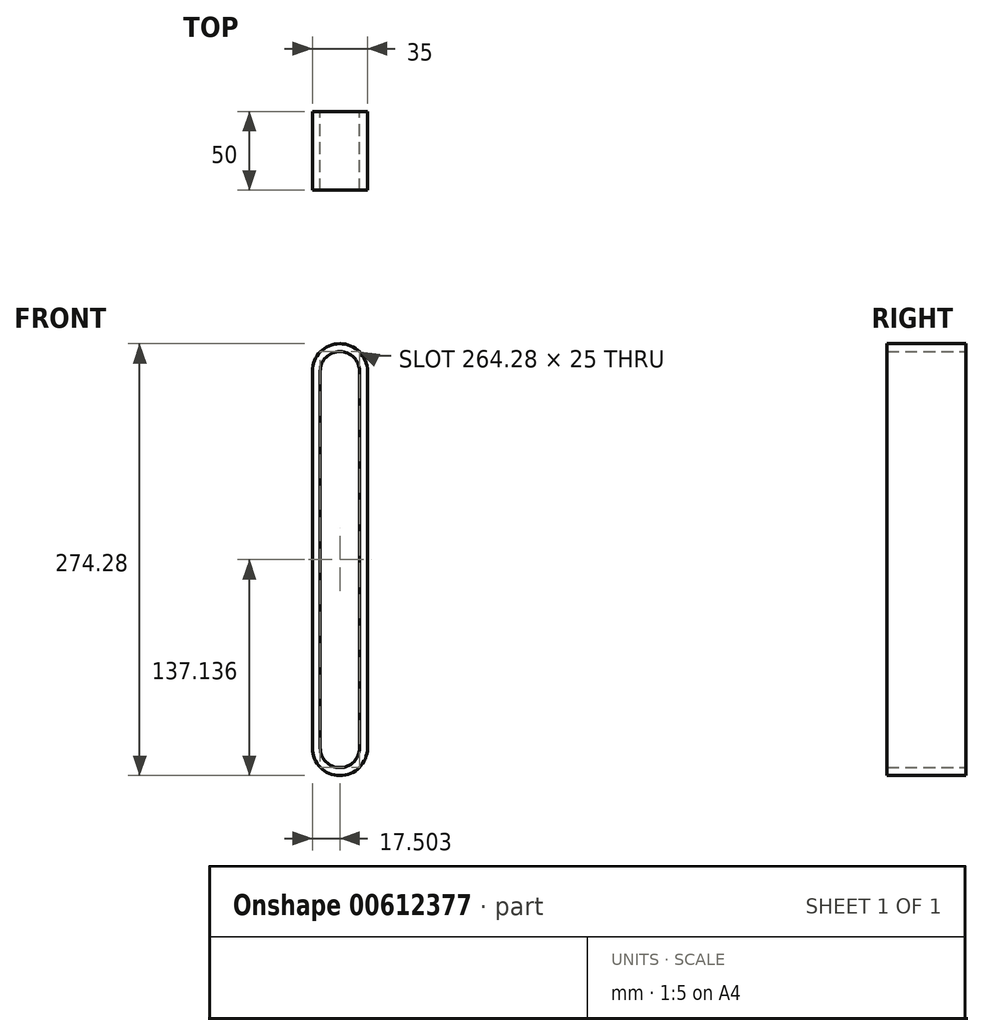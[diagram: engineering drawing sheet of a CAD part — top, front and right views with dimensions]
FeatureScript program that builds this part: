
annotation { "Feature Type Name" : "Feature", "Feature Type Description" : "" }
export const myFeature = defineFeature(function(context is Context, id is Id, definition is map)
    precondition{}
    {
        {
            var Q0;
            Q0=qCreatedBy(makeId("Front.planeOp"),FACE);
            var sketch = newSketch(context, id + "F0", { "sketchPlane" : qUnion([Q0])});
            skArc(sketch, "E0.0", {"start": v(17.65, 119.03) * mm, "mid": v(0.15, 136.53) * mm, "end": v(-17.35, 119.03) * mm});
            skLineSegment(sketch, "E0.1", {"start": v(17.65, 119.03) * mm, "end": v(17.65, -120.25) * mm});
            skArc(sketch, "E0.2", {"start": v(-17.35, -120.25) * mm, "mid": v(0.15, -137.75) * mm, "end": v(17.65, -120.25) * mm});
            skLineSegment(sketch, "E0.3", {"start": v(-17.35, 119.03) * mm, "end": v(-17.35, -120.25) * mm});
            skArc(sketch, "E1.0", {"start": v(12.65, 119.03) * mm, "mid": v(0.15, 131.53) * mm, "end": v(-12.35, 119.03) * mm});
            skLineSegment(sketch, "E1.1", {"start": v(12.65, 119.03) * mm, "end": v(12.65, -120.25) * mm});
            skArc(sketch, "E1.2", {"start": v(-12.35, -120.25) * mm, "mid": v(0.15, -132.75) * mm, "end": v(12.65, -120.25) * mm});
            skLineSegment(sketch, "E1.3", {"start": v(-12.35, 119.03) * mm, "end": v(-12.35, -120.25) * mm});
            skSolve(sketch);
        }
        {
            var Q0;
            Q0 = qSketchRegion(id + "F0", true);
            extrude(context, id + "F1", {"entities" : qUnion([Q0]), "depth" : 50 * mm, "offsetDistance" : 25 * mm});
        }
    });
